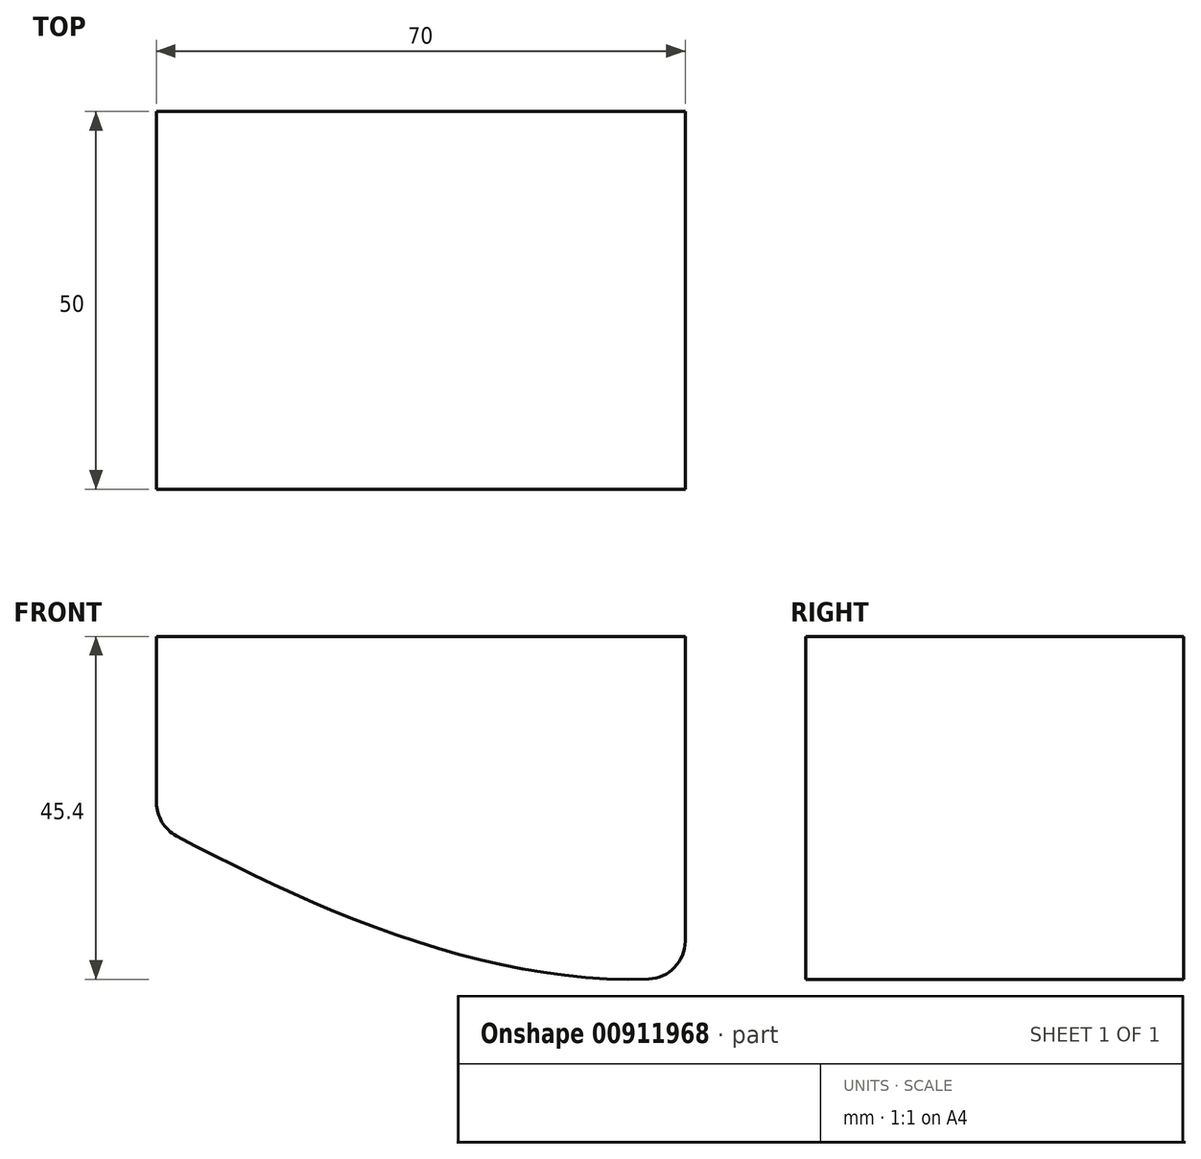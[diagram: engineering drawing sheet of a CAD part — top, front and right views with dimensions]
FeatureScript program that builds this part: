
annotation { "Feature Type Name" : "Feature", "Feature Type Description" : "" }
export const myFeature = defineFeature(function(context is Context, id is Id, definition is map)
    precondition{}
    {
        {
            var Q0;
            Q0=qCreatedBy(makeId("Front.planeOp"),FACE);
            var sketch = newSketch(context, id + "F0", { "sketchPlane" : qUnion([Q0])});
            skLineSegment(sketch, "E0", {"start": v(0, 0) * mm, "end": v(0, 25) * mm});
            skLineSegment(sketch, "E1", {"start": v(0, 25) * mm, "end": v(70, 25) * mm});
            skLineSegment(sketch, "E2", {"start": v(70, 25) * mm, "end": v(70, -20) * mm});
            skFitSpline(sketch, "E3", {"points": [v(0, 0) * mm, v(70, -20) * mm], "startDerivative": vector(62.96, -34.18) * mm, "endDerivative": vector(70.74, 8.1) * mm});
            skSolve(sketch);
        }
        {
            var Q0;
            Q0 = qSketchRegion(id + "F0", true);
            extrude(context, id + "F1", {"entities" : qUnion([Q0]), "depth" : 50 * mm, "offsetDistance" : 25 * mm});
        }
        {
            var Q0;
            Q0=makeQuery(id+"F1.opExtrude","SWEPT_EDGE",EDGE,{"disambiguationData":[OSD([sQuery(id+"F0.wireOp",EDGE,"E2"),sQuery(id+"F0.wireOp",EDGE,"E3")])]});
            var Q1;
            Q1=makeQuery(id+"F1.opExtrude","SWEPT_EDGE",EDGE,{"disambiguationData":[OSD([sQuery(id+"F0.wireOp",EDGE,"E0"),sQuery(id+"F0.wireOp",EDGE,"E3")])]});
            fillet(context, id + "F2", {"entities" : qUnion([Q0, Q1]), "radius" : 5 * mm, "tangentPropagation" : true, "allowEdgeOverflow" : false});
        }
    });
